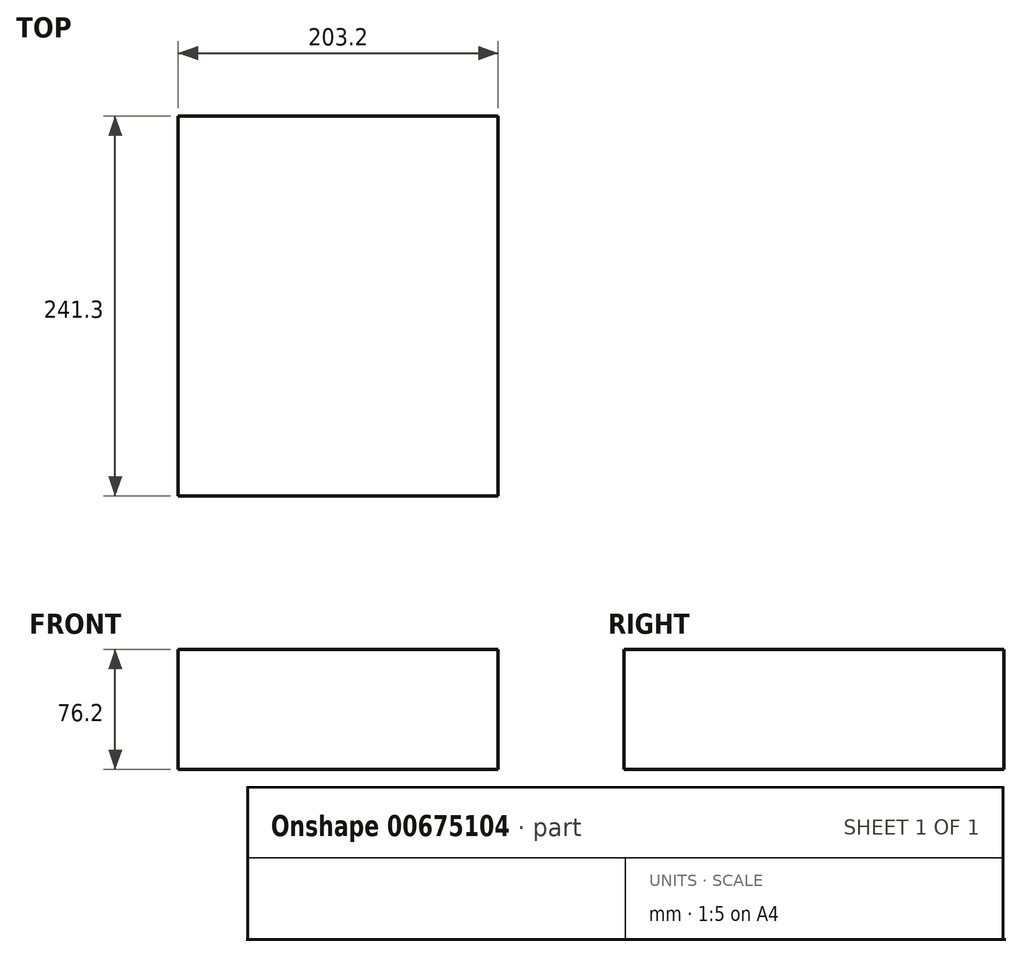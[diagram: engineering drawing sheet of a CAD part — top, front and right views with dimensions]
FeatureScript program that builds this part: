
annotation { "Feature Type Name" : "Feature", "Feature Type Description" : "" }
export const myFeature = defineFeature(function(context is Context, id is Id, definition is map)
    precondition{}
    {
        {
            var Q0;
            Q0=qCreatedBy(makeId("Top.planeOp"),FACE);
            var sketch = newSketch(context, id + "F0", { "sketchPlane" : qUnion([Q0])});
            skLineSegment(sketch, "E0", {"start": v(-87.33, 48.14) * mm, "end": v(115.87, 48.14) * mm});
            skLineSegment(sketch, "E1", {"start": v(115.87, 48.14) * mm, "end": v(115.87, -193.16) * mm});
            skLineSegment(sketch, "E2", {"start": v(115.87, -193.16) * mm, "end": v(-87.33, -193.16) * mm});
            skLineSegment(sketch, "E3", {"start": v(-87.33, -193.16) * mm, "end": v(-87.33, 48.14) * mm});
            skSolve(sketch);
        }
        {
            var Q0;
            Q0 = qSketchRegion(id + "F0", true);
            var Q1;
            Q1=makeQuery(id+"F0.imprint","IMPRINT",FACE,{"disambiguationData":[TD([[makeQuery(id+"F0.imprint","IMPRINT",EDGE,{"derivedFrom":sQuery(id+"F0.wireOp",EDGE,"E0")}),-1.0]])]});
            extrude(context, id + "F1", {"entities" : qUnion([Q0, Q1]), "depth" : 76.2 * mm, "offsetDistance" : 25.4 * mm});
        }
    });
